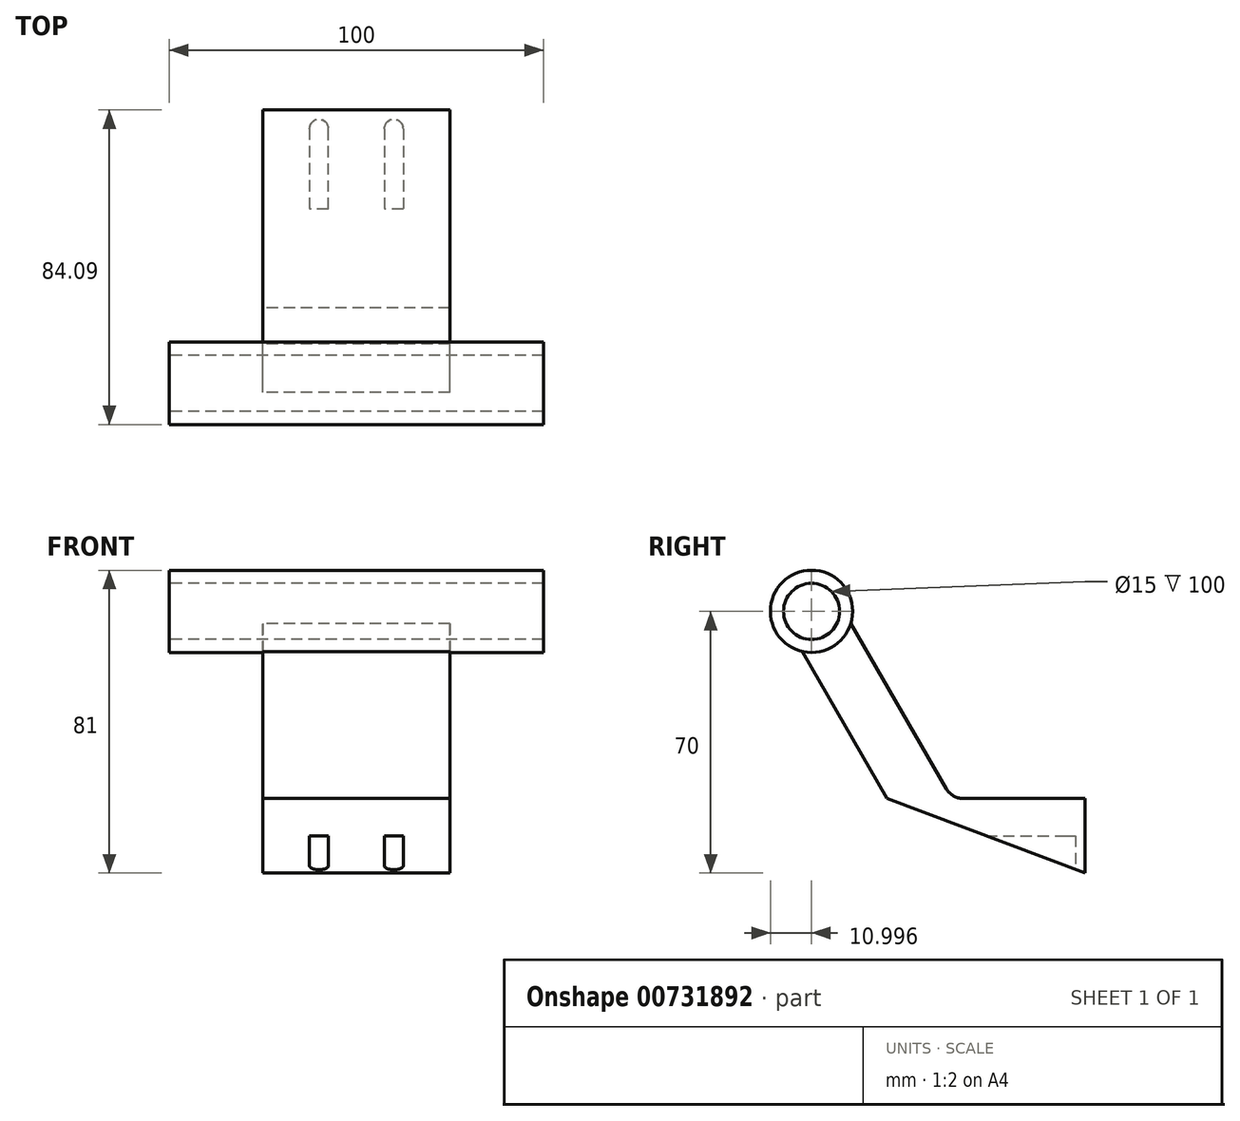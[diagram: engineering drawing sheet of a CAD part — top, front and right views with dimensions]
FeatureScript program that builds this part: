
annotation { "Feature Type Name" : "Feature", "Feature Type Description" : "" }
export const myFeature = defineFeature(function(context is Context, id is Id, definition is map)
    precondition{}
    {
        {
            var Q0;
            Q0=qCreatedBy(makeId("Right.planeOp"),FACE);
            var sketch = newSketch(context, id + "F0", { "sketchPlane" : qUnion([Q0])});
            skLineSegment(sketch, "E0", {"start": v(0, 0) * mm, "end": v(0, 20) * mm});
            skCircle(sketch, "E1", {"center": v(-73.1, 70) * mm, "radius": 11 * mm});
            skCircle(sketch, "E2", {"center": v(-73.1, 70) * mm, "radius": 7.5 * mm});
            skLineSegment(sketch, "E3", {"start": v(-66.6, 73.75) * mm, "end": v(-35.57, 20) * mm});
            skLineSegment(sketch, "E4", {"start": v(-79.59, 66.25) * mm, "end": v(-52.89, 20) * mm});
            skLineSegment(sketch, "E5", {"start": v(0, 0) * mm, "end": v(-52.89, 20) * mm});
            skLineSegment(sketch, "E6", {"start": v(0, 20) * mm, "end": v(-35.57, 20) * mm});
            skSolve(sketch);
        }
        {
            var Q0;
            Q0=makeQuery(id+"F0.imprint","IMPRINT",FACE,{"disambiguationData":[TD([[makeQuery(id+"F0.imprint","IMPRINT",EDGE,{"derivedFrom":sQuery(id+"F0.wireOp",EDGE,"E2")}),-1.0]])]});
            extrude(context, id + "F1", {"entities" : qUnion([Q0]), "endBound" : BoundingType.SYMMETRIC, "depth" : 100 * mm, "offsetDistance" : 25 * mm});
        }
        {
            var Q0;
            Q0=makeQuery(id+"F0.imprint","IMPRINT",FACE,{"disambiguationData":[TD([[makeQuery(id+"F0.imprint","IMPRINT",EDGE,{"derivedFrom":sQuery(id+"F0.wireOp",EDGE,"E0")}),1.0]])]});
            extrude(context, id + "F2", {"entities" : qUnion([Q0]), "operationType" : NewBodyOperationType.ADD, "endBound" : BoundingType.SYMMETRIC, "depth" : 50 * mm, "offsetDistance" : 25 * mm});
        }
        {
            var Q0;
            Q0=qCreatedBy(makeId("Top.planeOp"),FACE);
            var sketch = newSketch(context, id + "F3", { "sketchPlane" : qUnion([Q0])});
            skLineSegment(sketch, "E7", {"start": v(-12.53, -5) * mm, "end": v(-12.53, -30) * mm});
            skLineSegment(sketch, "E8", {"start": v(7.47, -5) * mm, "end": v(7.47, -30) * mm});
            skLineSegment(sketch, "E9", {"start": v(7.48, -30) * mm, "end": v(12.53, -30) * mm});
            skLineSegment(sketch, "E10", {"start": v(7.47, -5) * mm, "end": v(12.52, -5) * mm});
            skLineSegment(sketch, "E11", {"start": v(12.52, -5) * mm, "end": v(12.52, -30) * mm});
            skLineSegment(sketch, "E12", {"start": v(-12.53, -30) * mm, "end": v(-7.48, -30) * mm});
            skLineSegment(sketch, "E13", {"start": v(-12.53, -5) * mm, "end": v(-7.48, -5) * mm});
            skLineSegment(sketch, "E14", {"start": v(-7.48, -30) * mm, "end": v(-7.48, -5) * mm});
            skCircle(sketch, "E15", {"center": v(-10, -5) * mm, "radius": 2.52 * mm});
            skCircle(sketch, "E16", {"center": v(-10, -30) * mm, "radius": 2.52 * mm});
            skCircle(sketch, "E17", {"center": v(10, -5) * mm, "radius": 2.52 * mm});
            skCircle(sketch, "E18", {"center": v(10, -30) * mm, "radius": 2.53 * mm});
            skSolve(sketch);
        }
        {
            var Q0;
            Q0 = qSketchRegion(id + "F3", true);
            extrude(context, id + "F4", {"entities" : qUnion([Q0]), "operationType" : NewBodyOperationType.REMOVE, "depth" : 10 * mm, "offsetDistance" : 25 * mm});
        }
        {
            var Q0;
            Q0=makeQuery(id+"F2.opExtrude","SWEPT_EDGE",EDGE,{"disambiguationData":[OSD([sQuery(id+"F0.wireOp",EDGE,"E3"),sQuery(id+"F0.wireOp",EDGE,"E6")])]});
            fillet(context, id + "F5", {"entities" : qUnion([Q0]), "radius" : 5 * mm, "tangentPropagation" : true, "allowEdgeOverflow" : false});
        }
    });
